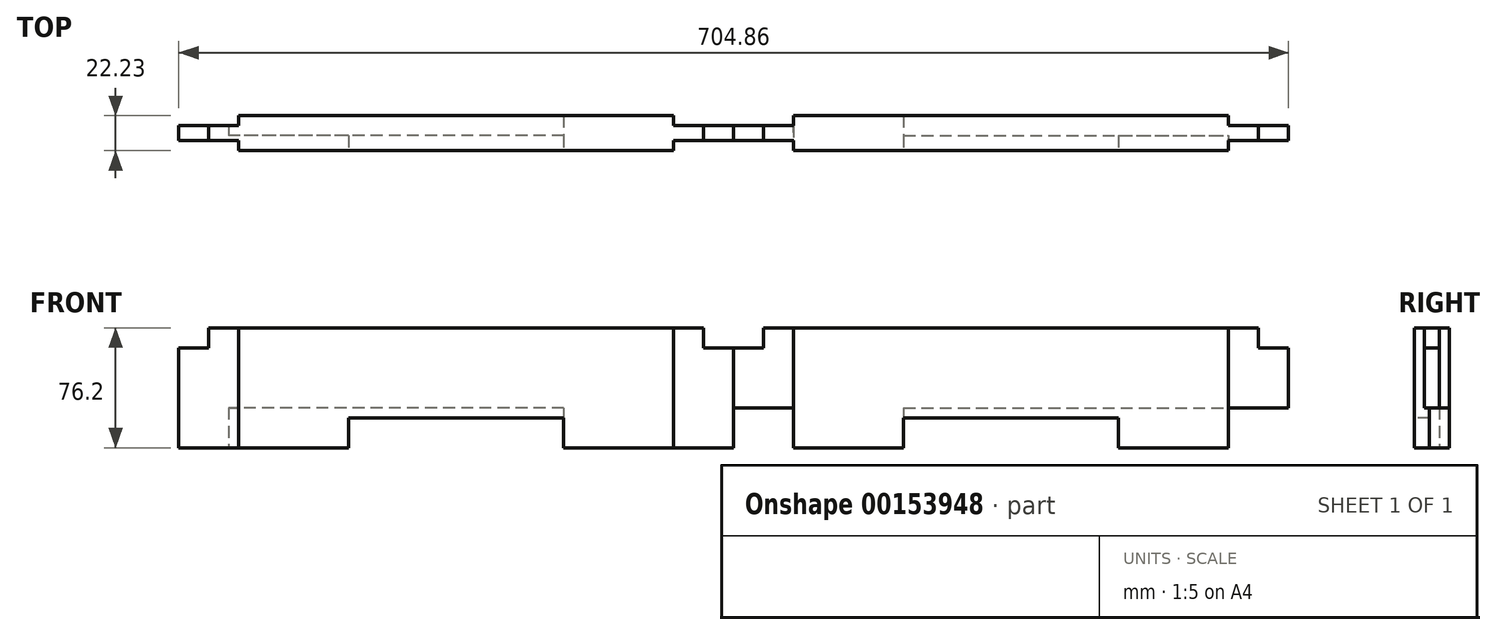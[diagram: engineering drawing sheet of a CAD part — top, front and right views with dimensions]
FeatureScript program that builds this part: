
annotation { "Feature Type Name" : "Feature", "Feature Type Description" : "" }
export const myFeature = defineFeature(function(context is Context, id is Id, definition is map)
    precondition{}
    {
        {
            var Q0;
            Q0=qCreatedBy(makeId("Front.planeOp"),FACE);
            var sketch = newSketch(context, id + "F0", { "sketchPlane" : qUnion([Q0])});
            skLineSegment(sketch, "E0.bottom", {"start": v(0, 0) * mm, "end": v(352.43, 0) * mm});
            skLineSegment(sketch, "E0.top", {"start": v(0, 76.2) * mm, "end": v(352.43, 76.2) * mm});
            skLineSegment(sketch, "E0.left", {"start": v(0, 0) * mm, "end": v(0, 76.2) * mm});
            skLineSegment(sketch, "E0.right", {"start": v(352.43, 0) * mm, "end": v(352.43, 76.2) * mm});
            skSolve(sketch);
        }
        {
            var Q0;
            Q0=makeQuery(id+"F0.imprint","IMPRINT",FACE,{"disambiguationData":[TD([[makeQuery(id+"F0.imprint","IMPRINT",EDGE,{"derivedFrom":sQuery(id+"F0.wireOp",EDGE,"E0.bottom")}),1.0]])]});
            extrude(context, id + "F1", {"entities" : qUnion([Q0]), "depth" : 22.22 * mm});
        }
        {
            var Q0;
            Q0=makeQuery(id+"F1.opExtrude","SWEPT_FACE",FACE,{"disambiguationData":[OSD([sQuery(id+"F0.wireOp",EDGE,"E0.bottom")])]});
            var sketch = newSketch(context, id + "F2", { "sketchPlane" : qUnion([Q0])});
            skLineSegment(sketch, "E1.bottom", {"start": v(0, 15.88) * mm, "end": v(352.43, 15.88) * mm});
            skLineSegment(sketch, "E1.top", {"start": v(0, 6.35) * mm, "end": v(352.43, 6.35) * mm});
            skLineSegment(sketch, "E1.left", {"start": v(0, 15.88) * mm, "end": v(0, 6.35) * mm});
            skLineSegment(sketch, "E1.right", {"start": v(352.43, 15.88) * mm, "end": v(352.43, 6.35) * mm});
            skLineSegment(sketch, "E2", {"start": v(38.1, 22.23) * mm, "end": v(38.1, 0) * mm});
            skLineSegment(sketch, "E3", {"start": v(314.33, 22.23) * mm, "end": v(314.33, 0) * mm});
            skSolve(sketch);
        }
        {
            var Q0;
            {var subQ1=sQuery(id+"F0.wireOp",EDGE,"E0.bottom");var subQ4=sQuery(id+"F2.wireOp",EDGE,"E2");var subQ6=makeQuery(id+"F1.opExtrude","CAP_EDGE",EDGE,{"disambiguationData":[OSD([subQ1])],"isStart":false});var subQ7=makeQuery(id+"F2.imprint","INTERSECT",VERTEX,{"derivedFrom":[subQ6,subQ4]});Q0=makeQuery(id+"F2.imprint","IMPRINT",FACE,{"disambiguationData":[TD([[makeQuery(id+"F2.imprint","IMPRINT",EDGE,{"disambiguationData":[TD([[subQ7,-1.0]])],"derivedFrom":subQ4}),-1.0]])]});}
            var Q1;
            {var subQ1=sQuery(id+"F0.wireOp",EDGE,"E0.bottom");var subQ4=sQuery(id+"F2.wireOp",EDGE,"E2");var subQ6=makeQuery(id+"F1.opExtrude","CAP_EDGE",EDGE,{"disambiguationData":[OSD([subQ1])],"isStart":true});var subQ7=makeQuery(id+"F2.imprint","INTERSECT",VERTEX,{"derivedFrom":[subQ6,subQ4]});Q1=makeQuery(id+"F2.imprint","IMPRINT",FACE,{"disambiguationData":[TD([[makeQuery(id+"F2.imprint","IMPRINT",EDGE,{"disambiguationData":[TD([[subQ7,1.0]])],"derivedFrom":subQ4}),-1.0]])]});}
            var Q2;
            {var subQ1=sQuery(id+"F0.wireOp",EDGE,"E0.bottom");var subQ4=sQuery(id+"F2.wireOp",EDGE,"E3");var subQ6=makeQuery(id+"F1.opExtrude","CAP_EDGE",EDGE,{"disambiguationData":[OSD([subQ1])],"isStart":false});var subQ7=makeQuery(id+"F2.imprint","INTERSECT",VERTEX,{"derivedFrom":[subQ6,subQ4]});Q2=makeQuery(id+"F2.imprint","IMPRINT",FACE,{"disambiguationData":[TD([[makeQuery(id+"F2.imprint","IMPRINT",EDGE,{"disambiguationData":[TD([[subQ7,-1.0]])],"derivedFrom":subQ4}),1.0]])]});}
            var Q3;
            {var subQ1=sQuery(id+"F0.wireOp",EDGE,"E0.bottom");var subQ4=sQuery(id+"F2.wireOp",EDGE,"E3");var subQ6=makeQuery(id+"F1.opExtrude","CAP_EDGE",EDGE,{"disambiguationData":[OSD([subQ1])],"isStart":true});var subQ7=makeQuery(id+"F2.imprint","INTERSECT",VERTEX,{"derivedFrom":[subQ6,subQ4]});Q3=makeQuery(id+"F2.imprint","IMPRINT",FACE,{"disambiguationData":[TD([[makeQuery(id+"F2.imprint","IMPRINT",EDGE,{"disambiguationData":[TD([[subQ7,1.0]])],"derivedFrom":subQ4}),1.0]])]});}
            extrude(context, id + "F3", {"entities" : qUnion([Q0, Q1, Q2, Q3]), "operationType" : NewBodyOperationType.REMOVE, "endBound" : BoundingType.UP_TO_NEXT, "oppositeDirection" : true, "depth" : 25.4 * mm});
        }
        {
            var Q0;
            {var subQ0=sQuery(id+"F2.wireOp",EDGE,"E1.bottom");Q0=makeQuery(id+"F3.boolean.opBoolean","COPY",FACE,{"derivedFrom":makeQuery(id+"F3.opExtrude","SWEPT_FACE",FACE,{"disambiguationData":[OSD([subQ0]),TDD([makeQuery(id+"F2.imprint","IMPRINT",EDGE,{"disambiguationData":[TD([[makeQuery(id+"F2.imprint","INTERSECT",VERTEX,{"derivedFrom":[subQ0,sQuery(id+"F2.wireOp",EDGE,"E2")]}),1.0]])],"derivedFrom":subQ0})])]})});}
            var sketch = newSketch(context, id + "F4", { "sketchPlane" : qUnion([Q0])});
            skLineSegment(sketch, "E4.bottom", {"start": v(0, 76.2) * mm, "end": v(19.05, 76.2) * mm});
            skLineSegment(sketch, "E4.top", {"start": v(0, 63.5) * mm, "end": v(19.05, 63.5) * mm});
            skLineSegment(sketch, "E4.left", {"start": v(0, 76.2) * mm, "end": v(0, 63.5) * mm});
            skLineSegment(sketch, "E4.right", {"start": v(19.05, 76.2) * mm, "end": v(19.05, 63.5) * mm});
            skLineSegment(sketch, "E5.bottom", {"start": v(333.38, 63.5) * mm, "end": v(352.43, 63.5) * mm});
            skLineSegment(sketch, "E5.top", {"start": v(333.38, 76.2) * mm, "end": v(352.43, 76.2) * mm});
            skLineSegment(sketch, "E5.left", {"start": v(333.38, 63.5) * mm, "end": v(333.38, 76.2) * mm});
            skLineSegment(sketch, "E5.right", {"start": v(352.43, 63.5) * mm, "end": v(352.43, 76.2) * mm});
            skSolve(sketch);
        }
        {
            var Q0;
            Q0=makeQuery(id+"F4.imprint","IMPRINT",FACE,{"disambiguationData":[TD([[makeQuery(id+"F4.imprint","IMPRINT",EDGE,{"derivedFrom":sQuery(id+"F4.wireOp",EDGE,"E4.bottom")}),-1.0]])]});
            var Q1;
            Q1=makeQuery(id+"F4.imprint","IMPRINT",FACE,{"disambiguationData":[TD([[makeQuery(id+"F4.imprint","IMPRINT",EDGE,{"derivedFrom":sQuery(id+"F4.wireOp",EDGE,"E5.bottom")}),1.0]])]});
            extrude(context, id + "F5", {"entities" : qUnion([Q0, Q1]), "operationType" : NewBodyOperationType.REMOVE, "endBound" : BoundingType.UP_TO_NEXT, "oppositeDirection" : true, "depth" : 25.4 * mm});
        }
        {
            var Q0;
            Q0=makeQuery(id+"F1.opExtrude","CAP_FACE",FACE,{"disambiguationData":[OSD([sQuery(id+"F0.wireOp",EDGE,"E0.bottom"),sQuery(id+"F0.wireOp",EDGE,"E0.top"),sQuery(id+"F0.wireOp",EDGE,"E0.left"),sQuery(id+"F0.wireOp",EDGE,"E0.right")])],"isStart":false});
            var sketch = newSketch(context, id + "F6", { "sketchPlane" : qUnion([Q0])});
            skLineSegment(sketch, "E6.bottom", {"start": v(107.95, 0) * mm, "end": v(244.47, 0) * mm});
            skLineSegment(sketch, "E6.top", {"start": v(107.95, 19.05) * mm, "end": v(244.47, 19.05) * mm});
            skLineSegment(sketch, "E6.left", {"start": v(107.95, 0) * mm, "end": v(107.95, 19.05) * mm});
            skLineSegment(sketch, "E6.right", {"start": v(244.47, 0) * mm, "end": v(244.47, 19.05) * mm});
            skSolve(sketch);
        }
        {
            var Q0;
            Q0=makeQuery(id+"F6.imprint","IMPRINT",FACE,{"disambiguationData":[TD([[makeQuery(id+"F6.imprint","IMPRINT",EDGE,{"derivedFrom":sQuery(id+"F6.wireOp",EDGE,"E6.bottom")}),1.0]])]});
            extrude(context, id + "F7", {"entities" : qUnion([Q0]), "operationType" : NewBodyOperationType.REMOVE, "endBound" : BoundingType.UP_TO_NEXT, "oppositeDirection" : true, "depth" : 25.4 * mm});
        }
        {
            var Q0;
            {var subQ2=sQuery(id+"F0.wireOp",EDGE,"E0.left");var subQ3=sQuery(id+"F0.wireOp",EDGE,"E0.bottom");Q0=makeQuery(id+"F7.boolean.opBoolean","SPLIT",FACE,{"disambiguationData":[TD([makeQuery(id+"F1.opExtrude","SWEPT_FACE",FACE,{"disambiguationData":[OSD([subQ2])]})])],"derivedFrom":makeQuery(id+"F1.opExtrude","SWEPT_FACE",FACE,{"disambiguationData":[OSD([subQ3])]})});}
            var sketch = newSketch(context, id + "F8", { "sketchPlane" : qUnion([Q0])});
            skLineSegment(sketch, "E7.bottom", {"start": v(31.75, 0) * mm, "end": v(320.68, 0) * mm});
            skLineSegment(sketch, "E7.top", {"start": v(31.75, 12.7) * mm, "end": v(320.68, 12.7) * mm});
            skLineSegment(sketch, "E7.left", {"start": v(31.75, 0) * mm, "end": v(31.75, 12.7) * mm});
            skLineSegment(sketch, "E7.right", {"start": v(320.68, 0) * mm, "end": v(320.68, 12.7) * mm});
            skSolve(sketch);
        }
        {
            var Q0;
            {var subQ4=sQuery(id+"F0.wireOp",EDGE,"E0.bottom");var subQ5=sQuery(id+"F2.wireOp",EDGE,"E2");var subQ9=makeQuery(id+"F3.boolean.opBoolean","COPY",EDGE,{"derivedFrom":makeQuery(id+"F3.opExtrude","CAP_EDGE",EDGE,{"disambiguationData":[OSD([subQ5]),TDD([makeQuery(id+"F2.imprint","IMPRINT",EDGE,{"disambiguationData":[TD([[makeQuery(id+"F2.imprint","INTERSECT",VERTEX,{"derivedFrom":[makeQuery(id+"F1.opExtrude","CAP_EDGE",EDGE,{"disambiguationData":[OSD([subQ4])],"isStart":true}),subQ5]}),1.0]])],"derivedFrom":subQ5})])],"isStart":true})});Q0=makeQuery(id+"F8.imprint","IMPRINT",FACE,{"disambiguationData":[TD([[makeQuery(id+"F8.imprint","IMPRINT",EDGE,{"derivedFrom":subQ9}),1.0]])]});}
            var Q1;
            {var subQ3=sQuery(id+"F8.wireOp",EDGE,"E7.right");Q1=makeQuery(id+"F8.imprint","IMPRINT",FACE,{"disambiguationData":[TD([[makeQuery(id+"F8.imprint","IMPRINT",EDGE,{"derivedFrom":subQ3}),1.0]])]});}
            extrude(context, id + "F9", {"entities" : qUnion([Q0, Q1]), "operationType" : NewBodyOperationType.REMOVE, "oppositeDirection" : true, "depth" : 25.4 * mm});
        }
        {
            var Q0;
            Q0=makeQuery(id+"F1.opExtrude","SWEPT_BODY",BODY,{"disambiguationData":[OSD([sQuery(id+"F0.wireOp",EDGE,"E0.bottom"),sQuery(id+"F0.wireOp",EDGE,"E0.top"),sQuery(id+"F0.wireOp",EDGE,"E0.left"),sQuery(id+"F0.wireOp",EDGE,"E0.right")])]});
            var Q1;
            Q1=qCreatedBy(makeId("Right.planeOp"),FACE);
            mirror(context, id + "F10", {"entities" : qUnion([Q0]), "mirrorPlane" : qUnion([Q1])});
        }
        {
            var Q0;
            {var subQ0=sQuery(id+"F2.wireOp",EDGE,"E1.bottom");Q0=makeQuery(id+"F3.boolean.opBoolean","COPY",FACE,{"derivedFrom":makeQuery(id+"F3.opExtrude","SWEPT_FACE",FACE,{"disambiguationData":[OSD([subQ0]),TDD([makeQuery(id+"F2.imprint","IMPRINT",EDGE,{"disambiguationData":[TD([[makeQuery(id+"F2.imprint","INTERSECT",VERTEX,{"derivedFrom":[subQ0,sQuery(id+"F2.wireOp",EDGE,"E2")]}),1.0]])],"derivedFrom":subQ0})])]})});}
            var sketch = newSketch(context, id + "F11", { "sketchPlane" : qUnion([Q0])});
            skLineSegment(sketch, "E8.bottom", {"start": v(0, 0) * mm, "end": v(38.1, 0) * mm});
            skLineSegment(sketch, "E8.top", {"start": v(0, 25.4) * mm, "end": v(38.1, 25.4) * mm});
            skLineSegment(sketch, "E8.left", {"start": v(0, 0) * mm, "end": v(0, 25.4) * mm});
            skLineSegment(sketch, "E8.right", {"start": v(38.1, 0) * mm, "end": v(38.1, 25.4) * mm});
            skLineSegment(sketch, "E9.bottom", {"start": v(352.43, 0) * mm, "end": v(314.33, 0) * mm});
            skLineSegment(sketch, "E9.top", {"start": v(352.43, 25.4) * mm, "end": v(314.33, 25.4) * mm});
            skLineSegment(sketch, "E9.left", {"start": v(352.43, 0) * mm, "end": v(352.43, 25.4) * mm});
            skLineSegment(sketch, "E9.right", {"start": v(314.33, 0) * mm, "end": v(314.33, 25.4) * mm});
            skSolve(sketch);
        }
        {
            var Q0;
            Q0=makeQuery(id+"F11.imprint","IMPRINT",FACE,{"disambiguationData":[TD([[makeQuery(id+"F11.imprint","IMPRINT",EDGE,{"derivedFrom":sQuery(id+"F11.wireOp",EDGE,"E8.bottom")}),1.0]])]});
            var Q1;
            Q1=makeQuery(id+"F11.imprint","IMPRINT",FACE,{"disambiguationData":[TD([[makeQuery(id+"F11.imprint","IMPRINT",EDGE,{"derivedFrom":sQuery(id+"F11.wireOp",EDGE,"E9.bottom")}),-1.0]])]});
            extrude(context, id + "F12", {"entities" : qUnion([Q0, Q1]), "operationType" : NewBodyOperationType.REMOVE, "endBound" : BoundingType.THROUGH_ALL, "oppositeDirection" : true, "depth" : 25.4 * mm});
        }
    });
